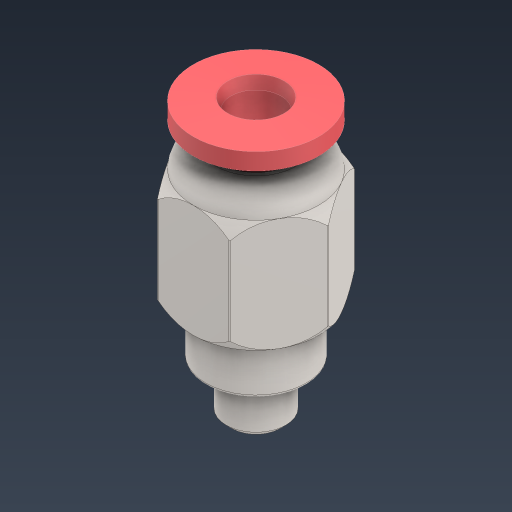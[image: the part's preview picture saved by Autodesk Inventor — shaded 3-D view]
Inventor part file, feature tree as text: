
AUTODESK INVENTOR PART (.ipt)
format: ipt  version: 2024.3 (Build 283343000, 343)  size: 323,584 bytes
history: native  units: in
note: dims shown in document units (in); Inventor stores cm internally (conversion verified against a paired STEP export)
features: other x1, revolve x1, chamfer x1, fillet x1
ambient origin geometry x8: Origin, YZ Plane, XZ Plane, XY Plane, X Axis, Y Axis, Z Axis, Center Point
bodies: Solid1 (feature_tree), Solid2 (feature_tree), Solid3 (feature_tree)
feature tree (4):
  other  "Straight Pneumatic Fitting1"
  revolve  "Revolve2"  [1 undecoded]
  chamfer  "Chamfer4"  [1 undecoded]
  fillet  "Fillet2"  [1 undecoded]
note: 3 required parameter values undecoded (feature->parameter linkage not recoverable at this tier; creation-order binding heuristic only, values carry confidence <= 0.55)
